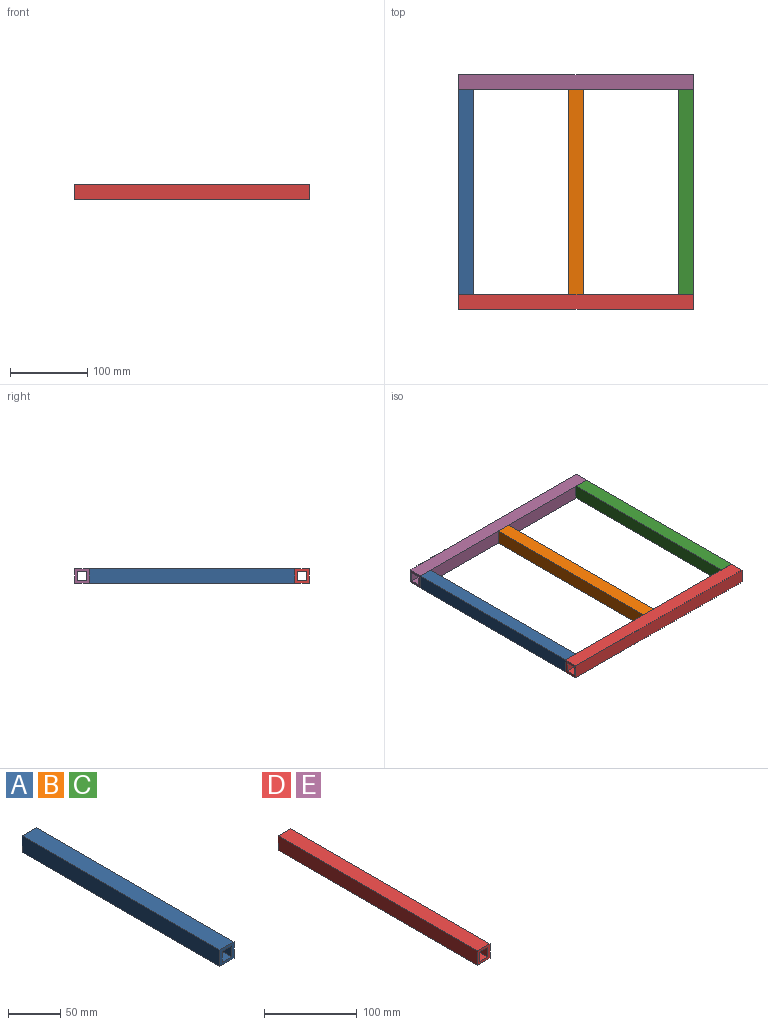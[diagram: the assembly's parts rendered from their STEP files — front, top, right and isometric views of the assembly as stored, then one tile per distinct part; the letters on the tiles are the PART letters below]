
ASSEMBLY  parts=5 mates=4
PART A: 10 faces, bbox 19.1x266.7x19.1 mm
  f0: plane 266.7x19.05mm, normal (0,0,1), area 5080.6mm2, adj f1,f7,f8,f9
  f1: plane 266.7x19.05mm, normal (-1,0,0), area 5080.6mm2, adj f0,f2,f8,f9
  f2: plane 266.7x19.05mm, normal (0,0,-1), area 5080.6mm2, adj f1,f7,f8,f9
  f3: plane 266.7x12.7mm, normal (-1,0,0), area 3387.1mm2, adj f4,f6,f8,f9
  f4: plane 266.7x12.7mm, normal (0,0,1), area 3387.1mm2, adj f3,f5,f8,f9
  f5: plane 266.7x12.7mm, normal (1,0,0), area 3387.1mm2, adj f4,f6,f8,f9
  f6: plane 266.7x12.7mm, normal (0,0,-1), area 3387.1mm2, adj f3,f5,f8,f9
  f7: plane 266.7x19.05mm, normal (1,0,0), area 5080.6mm2, adj f0,f2,f8,f9
  f8: plane 19.05x19.05mm, normal (0,-1,0), area 201.6mm2, adj f0,f1,f2,f3,f4,f5,f6,f7
  f9: plane 19.05x19.05mm, normal (0,1,0), area 201.6mm2, adj f0,f1,f2,f3,f4,f5,f6,f7
PART B: same geometry as A
PART C: same geometry as A
PART D: 10 faces, bbox 19.1x304.8x19.1 mm
  f0: plane 304.8x19.05mm, normal (0,0,1), area 5806.4mm2, adj f1,f7,f8,f9
  f1: plane 304.8x19.05mm, normal (-1,0,0), area 5806.4mm2, adj f0,f2,f8,f9
  f2: plane 304.8x19.05mm, normal (0,0,-1), area 5806.4mm2, adj f1,f7,f8,f9
  f3: plane 304.8x12.7mm, normal (-1,0,0), area 3871mm2, adj f4,f6,f8,f9
  f4: plane 304.8x12.7mm, normal (0,0,1), area 3871mm2, adj f3,f5,f8,f9
  f5: plane 304.8x12.7mm, normal (1,0,0), area 3871mm2, adj f4,f6,f8,f9
  f6: plane 304.8x12.7mm, normal (0,0,-1), area 3871mm2, adj f3,f5,f8,f9
  f7: plane 304.8x19.05mm, normal (1,0,0), area 5806.4mm2, adj f0,f2,f8,f9
  f8: plane 19.05x19.05mm, normal (0,-1,0), area 201.6mm2, adj f0,f1,f2,f3,f4,f5,f6,f7
  f9: plane 19.05x19.05mm, normal (0,1,0), area 201.6mm2, adj f0,f1,f2,f3,f4,f5,f6,f7
PART E: same geometry as D
PLACE A t=(-43.5,47.53,-113.99)mm
PLACE B t=(99.38,47.53,-113.99)mm
PLACE C t=(242.25,47.53,-113.99)mm
PLACE D rot(axis=(-0.58,-0.58,-0.58),120deg) t=(251.78,-228.7,-113.99)mm
PLACE E rot(axis=(0,0,-1),90deg) t=(251.78,57.05,-113.99)mm
MATE fastened A.f8 <-> D.f0  axis (0,-1,0) through (-53.02,-219.17,-123.51)mm
MATE fastened C.f8 <-> D.f0  axis (0,-1,0) through (251.78,-219.17,-123.51)mm
MATE fastened B.f8 <-> D.f0  axis (0,-1,0) through (99.38,-219.17,-104.46)mm
MATE fastened A.f9 <-> E.f7  axis (0,1,0) through (-53.02,47.53,-123.51)mm
